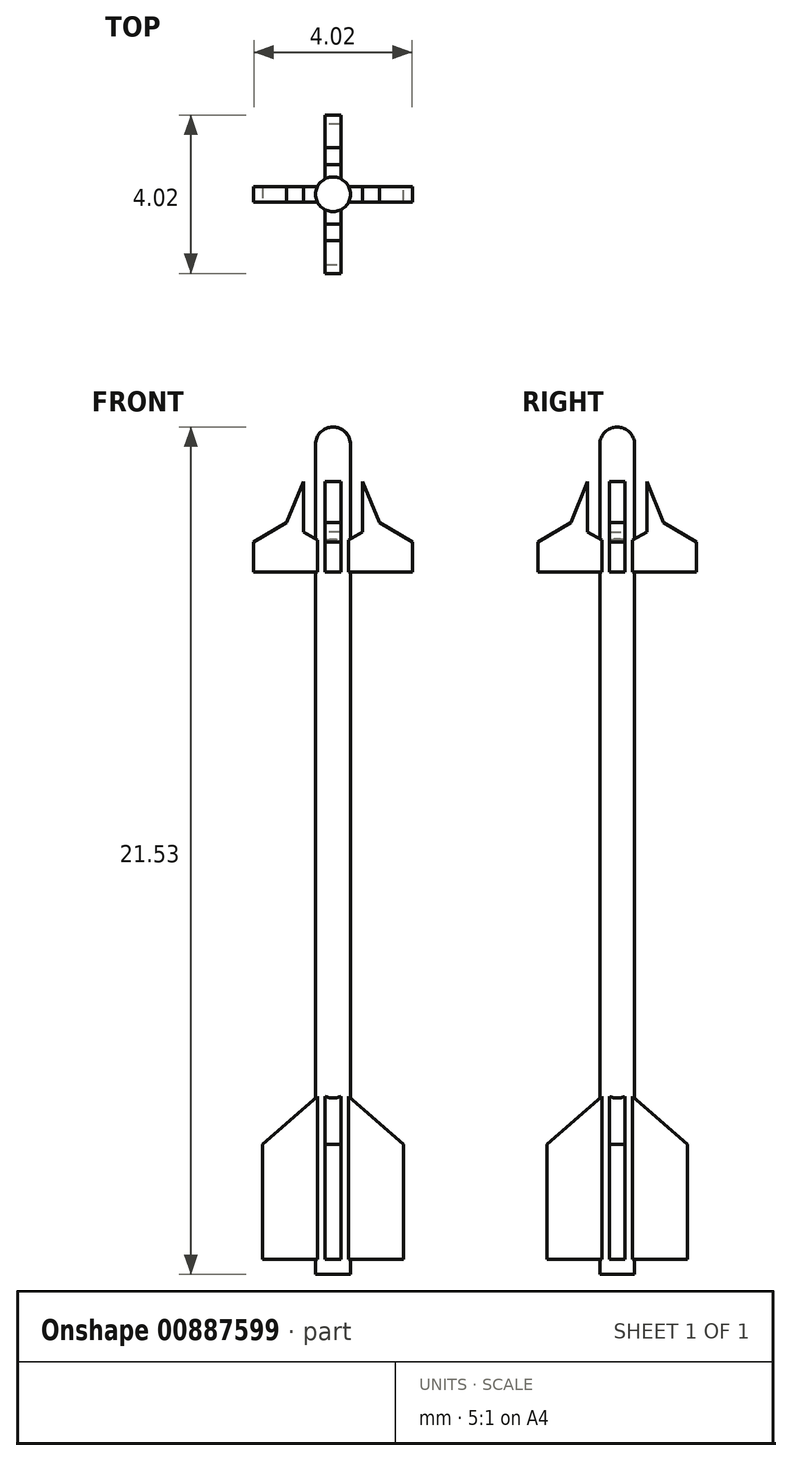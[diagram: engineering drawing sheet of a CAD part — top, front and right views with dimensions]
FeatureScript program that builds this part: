
annotation { "Feature Type Name" : "Feature", "Feature Type Description" : "" }
export const myFeature = defineFeature(function(context is Context, id is Id, definition is map)
    precondition{}
    {
        {
            var Q0;
            Q0=qCreatedBy(makeId("Front.planeOp"),FACE);
            var sketch = newSketch(context, id + "F0", { "sketchPlane" : qUnion([Q0])});
            skLineSegment(sketch, "E0", {"start": v(0, 0) * mm, "end": v(0, 21.53) * mm});
            skLineSegment(sketch, "E1", {"start": v(0.44, 21.09) * mm, "end": v(0.44, 0) * mm});
            skLineSegment(sketch, "E2", {"start": v(0.44, 0) * mm, "end": v(0, 0) * mm});
            skArc(sketch, "E3", {"start": v(0.44, 21.09) * mm, "mid": v(0.31, 21.4) * mm, "end": v(0, 21.53) * mm});
            skSolve(sketch);
        }
        {
            var Q0;
            {var subQ0=sQuery(id+"F0.wireOp",EDGE,"mrwio9nY-PsAZ-Zbfy-NhIU-sYq0QVbgGXAG");Q0=makeQuery(id+"F0.imprint","IMPRINT",FACE,{"disambiguationData":[TD([[makeQuery(id+"F0.imprint","IMPRINT",EDGE,{"derivedFrom":subQ0}),-1.0]])]});}
            var Q1;
            Q1=makeQuery(id+"F0.imprint","IMPRINT",FACE,{"disambiguationData":[TD([[makeQuery(id+"F0.imprint","IMPRINT",EDGE,{"derivedFrom":sQuery(id+"F0.wireOp",EDGE,"rEedh4zr-IGRr-Hqzj-sDLB-QnI7VE1V64O6.bottom")}),-1.0]])]});
            var Q2;
            Q2=makeQuery(id+"F0.imprint","IMPRINT",FACE,{"disambiguationData":[TD([[makeQuery(id+"F0.imprint","IMPRINT",EDGE,{"derivedFrom":sQuery(id+"F0.wireOp",EDGE,"E0")}),-1.0]])]});
            var Q3;
            Q3=makeQuery(id+"F0.imprint","IMPRINT",FACE,{"disambiguationData":[TD([[makeQuery(id+"F0.imprint","IMPRINT",EDGE,{"derivedFrom":sQuery(id+"F0.wireOp",EDGE,"p5wuz8j9-3HT4-kWwn-DjtP-lJmqTNSXSBJY.bottom")}),-1.0]])]});
            var Q4;
            Q4=sQuery(id+"F0.wireOp",EDGE,"E0");
            revolve(context, id + "F1", {"surfaceOperationType" : NewSurfaceOperationType.NEW, "entities" : qUnion([Q0, Q1, Q2, Q3]), "axis" : qUnion([Q4]), "revolveType" : RevolveType.FULL});
        }
        {
            var Q0;
            Q0=qCreatedBy(makeId("Front.planeOp"),FACE);
            var sketch = newSketch(context, id + "F2", { "sketchPlane" : qUnion([Q0])});
            skLineSegment(sketch, "E4", {"start": v(0, 0) * mm, "end": v(0, 22.29) * mm});
            skLineSegment(sketch, "E5", {"start": v(0.44, -0.2) * mm, "end": v(0.44, 32.87) * mm, "construction": true});
            skLineSegment(sketch, "E6.0", {"start": v(0.44, 0) * mm, "end": v(-0.44, 0) * mm});
            skLineSegment(sketch, "E7", {"start": v(0.44, -0.2) * mm, "end": v(0.44, 0) * mm});
            skLineSegment(sketch, "E8", {"start": v(0, 17.85) * mm, "end": v(2.01, 17.85) * mm});
            skLineSegment(sketch, "E9", {"start": v(0, 0.38) * mm, "end": v(1.79, 0.38) * mm});
            skLineSegment(sketch, "E10", {"start": v(0, 4.87) * mm, "end": v(1.79, 3.3) * mm});
            skPoint(sketch, "E11", {"position": v(0.44, 4.48) * mm});
            skLineSegment(sketch, "E12", {"start": v(1.79, 3.3) * mm, "end": v(1.79, 0.38) * mm});
            skLineSegment(sketch, "E13", {"start": v(2.01, 17.85) * mm, "end": v(2.01, 18.61) * mm});
            skLineSegment(sketch, "E14", {"start": v(2.01, 18.61) * mm, "end": v(1.18, 19.1) * mm});
            skLineSegment(sketch, "E15", {"start": v(1.18, 19.1) * mm, "end": v(0.75, 20.14) * mm});
            skLineSegment(sketch, "E16", {"start": v(0.75, 20.14) * mm, "end": v(0.75, 18.85) * mm});
            skLineSegment(sketch, "E17", {"start": v(0.75, 18.85) * mm, "end": v(0, 18.44) * mm});
            skPoint(sketch, "E18", {"position": v(0.44, 18.68) * mm});
            skSolve(sketch);
        }
        {
            var Q0;
            Q0=qSketchRegion(id+"F2",true);
            extrude(context, id + "F3", {"entities" : qUnion([Q0]), "operationType" : NewBodyOperationType.ADD, "depth" : .4 * mm, "offsetDistance" : 25 * mm, "symmetric" : true});
        }
        {
            var Q0;
            Q0=makeQuery(id+"F1.opRevolve","SWEPT_BODY",BODY,{"disambiguationData":[OSD([sQuery(id+"F0.wireOp",EDGE,"E0"),sQuery(id+"F0.wireOp",EDGE,"E1"),sQuery(id+"F0.wireOp",EDGE,"E2"),sQuery(id+"F0.wireOp",EDGE,"2EiOItwe-9FNA-eY8p-DkXH-AMy5AHyUmzZA"),sQuery(id+"F0.wireOp",EDGE,"lF35QjYl-MEgV-fRWE-0Yr6-Bt5vS8A7brRf")])]});
            var Q1;
            Q1=makeQuery(id+"F1.opRevolve","SWEPT_FACE",FACE,{"disambiguationData":[OSD([sQuery(id+"F0.wireOp",EDGE,"E1")])]});
            circularPattern(context, id + "F4", {"operationType" : NewBodyOperationType.ADD, "entities" : qUnion([Q0]), "axis" : qUnion([Q1]), "angle" : 360 * degree, "instanceCount" : 4, "equalSpace" : true, "computeTransformsWithoutBuiltin" : true});
        }
    });
